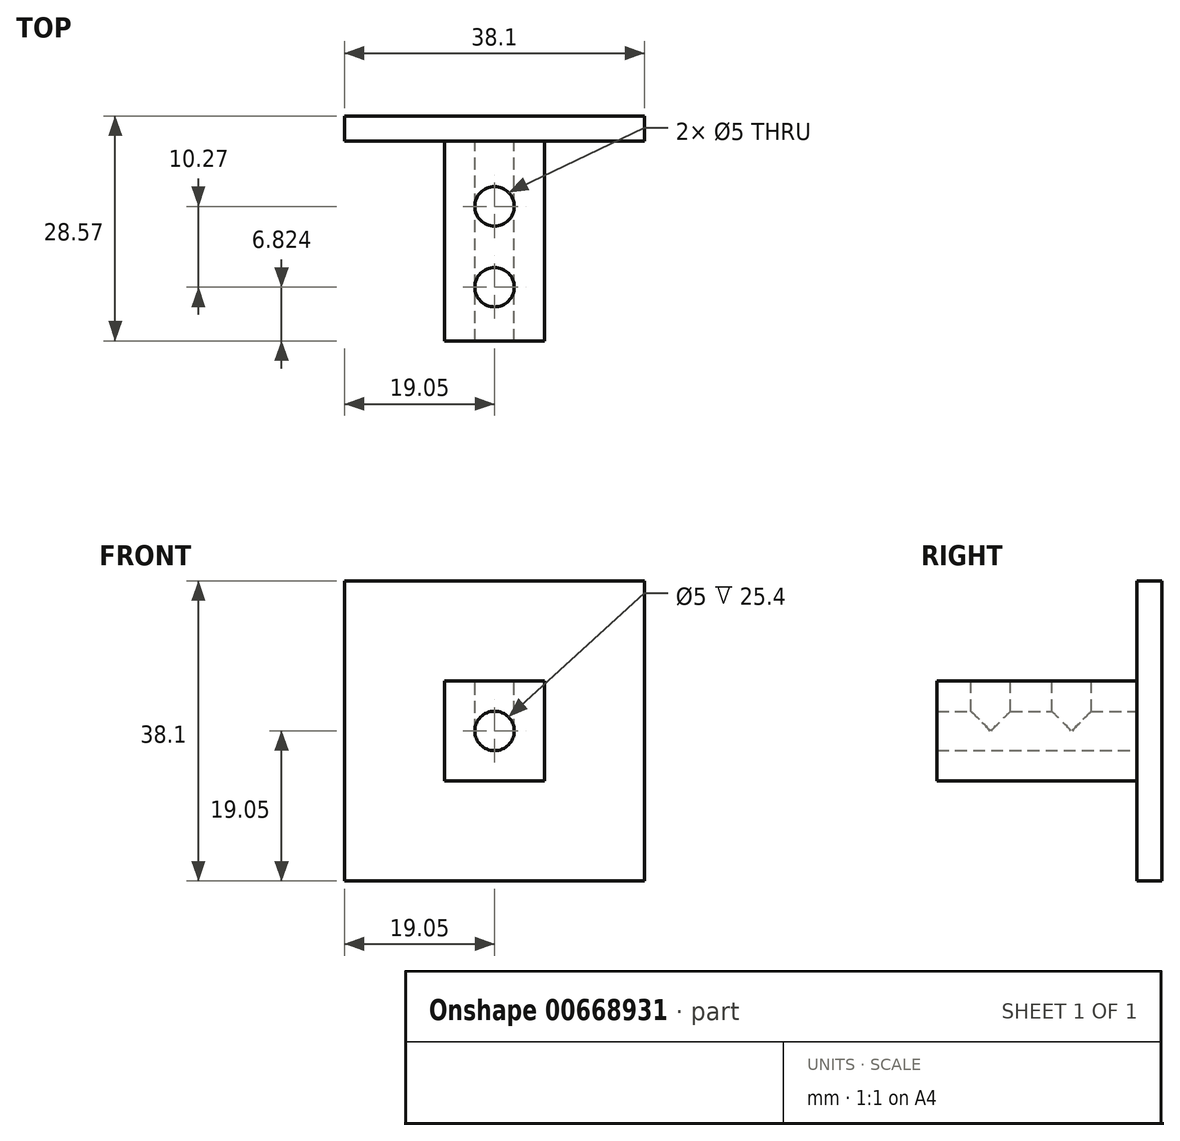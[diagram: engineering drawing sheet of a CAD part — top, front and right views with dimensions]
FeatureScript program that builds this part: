
annotation { "Feature Type Name" : "Feature", "Feature Type Description" : "" }
export const myFeature = defineFeature(function(context is Context, id is Id, definition is map)
    precondition{}
    {
        {
            var Q0;
            Q0=qCreatedBy(makeId("Front.planeOp"),FACE);
            var sketch = newSketch(context, id + "F0", { "sketchPlane" : qUnion([Q0])});
            skLineSegment(sketch, "E0.bottom", {"start": v(19.05, 19.05) * mm, "end": v(-19.05, 19.05) * mm});
            skLineSegment(sketch, "E0.top", {"start": v(19.05, -19.05) * mm, "end": v(-19.05, -19.05) * mm});
            skLineSegment(sketch, "E0.left", {"start": v(19.05, 19.05) * mm, "end": v(19.05, -19.05) * mm});
            skLineSegment(sketch, "E0.right", {"start": v(-19.05, 19.05) * mm, "end": v(-19.05, -19.05) * mm});
            skPoint(sketch, "E0.middle", {"position": v(0, 0) * mm});
            skSolve(sketch);
        }
        {
            var Q0;
            Q0 = qSketchRegion(id + "F0", true);
            extrude(context, id + "F1", {"entities" : qUnion([Q0]), "oppositeDirection" : true, "depth" : 3.17 * mm, "offsetDistance" : 25.4 * mm});
        }
        {
            var Q0;
            Q0=makeQuery(id+"F1.opExtrude","CAP_FACE",FACE,{"disambiguationData":[OSD([sQuery(id+"F0.wireOp",EDGE,"E0.bottom"),sQuery(id+"F0.wireOp",EDGE,"E0.top"),sQuery(id+"F0.wireOp",EDGE,"E0.left"),sQuery(id+"F0.wireOp",EDGE,"E0.right")])],"isStart":true});
            var sketch = newSketch(context, id + "F2", { "sketchPlane" : qUnion([Q0])});
            skLineSegment(sketch, "E1.bottom", {"start": v(6.35, 6.35) * mm, "end": v(-6.35, 6.35) * mm});
            skLineSegment(sketch, "E1.top", {"start": v(6.35, -6.35) * mm, "end": v(-6.35, -6.35) * mm});
            skLineSegment(sketch, "E1.left", {"start": v(6.35, 6.35) * mm, "end": v(6.35, -6.35) * mm});
            skLineSegment(sketch, "E1.right", {"start": v(-6.35, 6.35) * mm, "end": v(-6.35, -6.35) * mm});
            skPoint(sketch, "E1.middle", {"position": v(0, 0) * mm});
            skCircle(sketch, "E2", {"center": v(0, 0) * mm, "radius": 2.5 * mm});
            skSolve(sketch);
        }
        {
            var Q0;
            Q0 = qSketchRegion(id + "F2", true);
            extrude(context, id + "F3", {"entities" : qUnion([Q0]), "operationType" : NewBodyOperationType.ADD, "depth" : 25.4 * mm, "offsetDistance" : 25.4 * mm});
        }
        {
            var Q0;
            Q0=makeQuery(id+"F3.opExtrude","SWEPT_FACE",FACE,{"disambiguationData":[OSD([sQuery(id+"F2.wireOp",EDGE,"E1.bottom")])]});
            var sketch = newSketch(context, id + "F4", { "sketchPlane" : qUnion([Q0])});
            skLineSegment(sketch, "E3", {"start": v(0, 0) * mm, "end": v(0, -25.4) * mm});
            skCircle(sketch, "E4", {"center": v(0, -18.58) * mm, "radius": 2.5 * mm});
            skCircle(sketch, "E5", {"center": v(0, -8.3) * mm, "radius": 2.5 * mm});
            skSolve(sketch);
        }
        {
            var Q0;
            Q0 = qSketchRegion(id + "F4", true);
            extrude(context, id + "F5", {"entities" : qUnion([Q0]), "operationType" : NewBodyOperationType.REMOVE, "oppositeDirection" : true, "depth" : 6.35 * mm, "offsetDistance" : 25.4 * mm});
        }
    });
